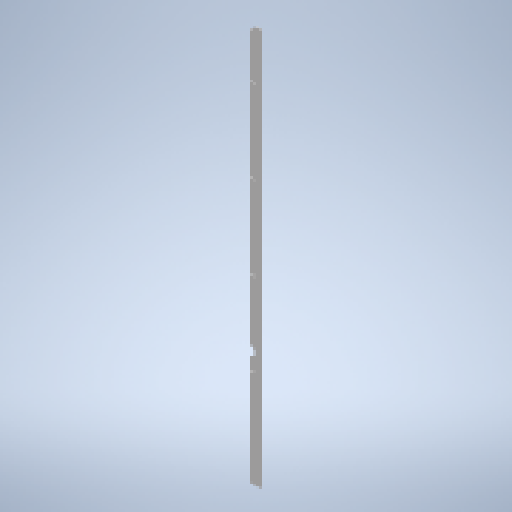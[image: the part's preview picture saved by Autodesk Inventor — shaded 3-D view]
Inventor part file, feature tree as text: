
AUTODESK INVENTOR PART (.ipt)
format: ipt  version: 2025 (Build 290162010, 162A)  size: 776,704 bytes
history: native  units: mm
features: other x4, sketch x4, projected_geometry x3, extrude x2, pattern_linear x2, sheet_metal_op x1
ambient origin geometry x8: Origin, YZ Plane, XZ Plane, XY Plane, X Axis, Y Axis, Z Axis, Center Point
bodies: Body1 (feature_tree)
feature tree (16):
  sheet_metal_op  "Face2"
  other  "Mark1"
  extrude  "Extrusion2"  Depth=2100.0mm
  pattern_linear  "Rectangular Pattern1"  Spacing1=232.0mm  [1 undecoded]
  extrude  "Extrusion3"  TaperAngle=0.0deg  [1 undecoded]
  pattern_linear  "Rectangular Pattern2"  Count1=5  [1 undecoded]
  other  "Corner Chamfer1"
  sketch  "Sketch6"  dims[d26=60.107271mm d27=2100.0mm]
  other  "Plate4"
  sketch  "Sketch7"  dims[d28=3.0mm]
  projected_geometry  "Projected Loop1"
  sketch  "Sketch8"  dims[d29=31.053636mm]
  projected_geometry  "Projected Loop2"
  sketch  "Sketch9"  dims[d30=3.2mm d31=232.0mm d32=0.0mm d33=0.0mm d34=50.0mm d36=500.0mm d37=50.0mm d38=620.0mm d39=0.0mm d40=0.0mm d41=20.0mm d43=1480.0mm d44=200.0mm d45=15.0mm d46=10.0mm d47=10.0mm d48=6.0mm d49=6.0mm d50=45.0deg]
  projected_geometry  "Projected Loop3"
  other  "Definition1"
note: 3 required parameter values undecoded (feature->parameter linkage not recoverable at this tier; creation-order binding heuristic only, values carry confidence <= 0.55)
